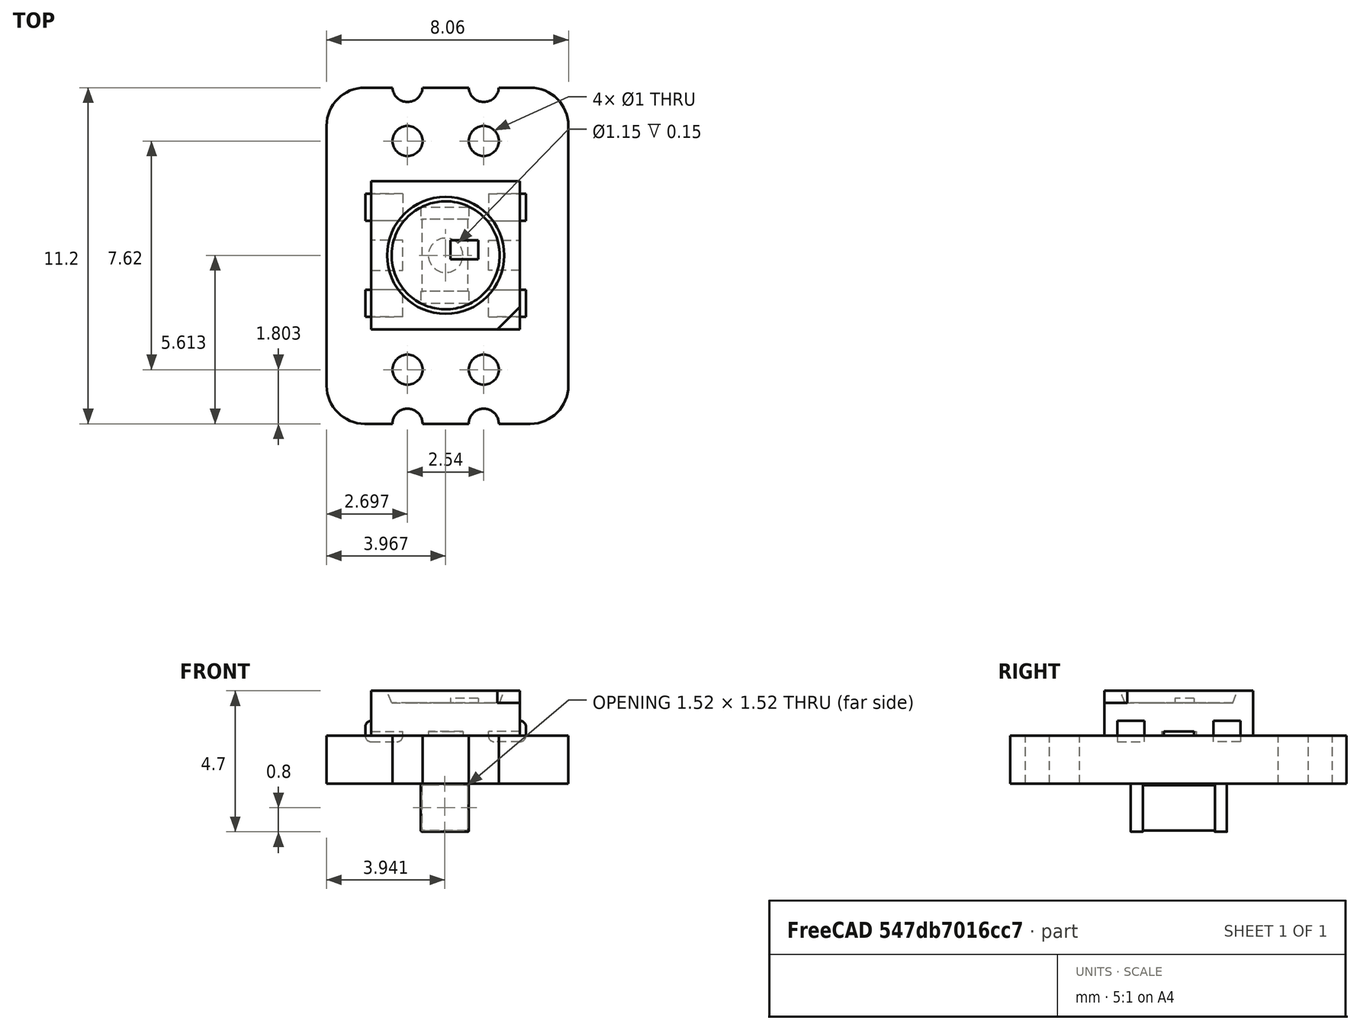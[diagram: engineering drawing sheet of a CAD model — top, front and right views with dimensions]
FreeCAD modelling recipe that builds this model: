
FCSTD DOCUMENT  (FreeCAD 0.16R6712 (Git))
Label: ws2812b_reverse
License: All rights reserved
LicenseURL: http://en.wikipedia.org/wiki/All_rights_reserved
objects: Part::Feature×3, App::DocumentObjectGroup×2, Sketcher::SketchObject×1
note: 4 computed .brp shape members not serialized (recipe doc carries the construction recipe); baked Part::Feature solids carry a one-line shape summary decoded from their .brp

FEATURE [Part::Feature] Pcb
  Placement = pos=(-144.208,107.328,0) rot=(0,0,1;0rad)
  shape: bbox 8.072 x 11.22 x 1.62 mm, 24 faces (baked)
FEATURE [Sketcher::SketchObject] PCB_Sketch
  sketch-geometry (8):
    g0: LineSegment StartX=4.0259 StartY=-4.3307 StartZ=0 EndX=4.0259 EndY=4.3307 EndZ=0
    g1: LineSegment StartX=-2.7559 StartY=-5.6007 StartZ=0 EndX=2.7559 EndY=-5.6007 EndZ=0
    g2: LineSegment StartX=-4.0259 StartY=4.3307 StartZ=0 EndX=-4.0259 EndY=-4.3307 EndZ=0
    g3: LineSegment StartX=2.7559 StartY=5.6007 StartZ=0 EndX=-2.7559 EndY=5.6007 EndZ=0
    g4: ArcOfCircle CenterX=2.7559 CenterY=-4.3307 CenterZ=0 NormalX=0 NormalY=0 NormalZ=1 Radius=1.27 StartAngle=4.71239 EndAngle=6.28319
    g5: ArcOfCircle CenterX=-2.7559 CenterY=-4.3307 CenterZ=0 NormalX=0 NormalY=0 NormalZ=1 Radius=1.27 StartAngle=3.14159 EndAngle=4.71239
    g6: ArcOfCircle CenterX=-2.7559 CenterY=4.3307 CenterZ=0 NormalX=0 NormalY=0 NormalZ=1 Radius=1.27 StartAngle=1.5708 EndAngle=3.14159
    g7: ArcOfCircle CenterX=2.7559 CenterY=4.3307 CenterZ=0 NormalX=0 NormalY=0 NormalZ=1 Radius=1.27 StartAngle=0 EndAngle=1.5708
FEATURE [App::DocumentObjectGroup] Board_Geoms
  Group = -> [Pcb,PCB_Sketch]
FEATURE [Part::Feature] Shape  label="risk1E78E08Bni4a_"
  Placement = pos=(-0.0635,0.0127,0) rot=(0,0,-1;1.5708rad)
  shape: bbox 5.35 x 4.95 x 1.7 mm, 58 faces (baked)
FEATURE [Part::Feature] Shape001  label="C_1206_3216Metric_"
  Placement = pos=(-0.0889,0.0127,-1.6) rot=(-0.707107,0.707107,0;3.14159rad)
  shape: bbox 1.6 x 3.2 x 1.6 mm, 28 faces (baked)
FEATURE [App::DocumentObjectGroup] Step_Models
  Group = -> [Shape,Shape001]
